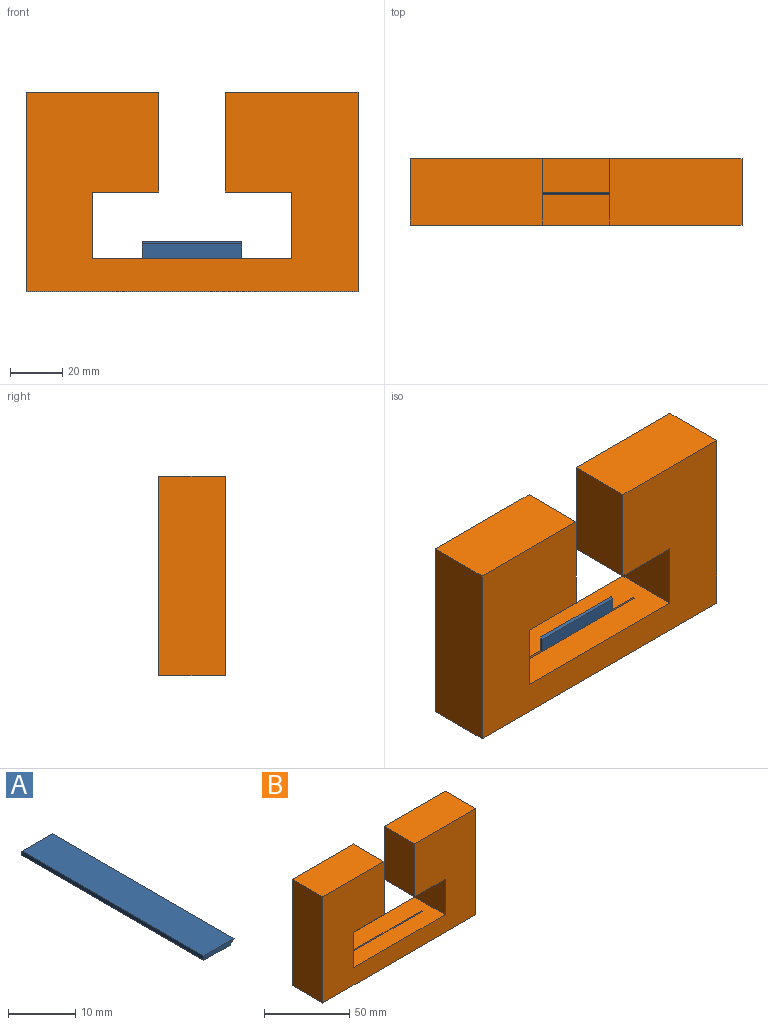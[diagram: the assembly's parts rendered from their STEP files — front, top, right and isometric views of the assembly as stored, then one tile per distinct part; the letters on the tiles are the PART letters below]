
ASSEMBLY  parts=2 mates=1
PART A: 7 faces, bbox 6.4x38.1x0.8 mm
  f0: plane 38.1x0.79mm, normal (-1,0,0), area 30.2mm2, adj f1,f3,f4,f5
  f1: plane 6.35x0.79mm, normal (0,-1,0), area 4.7mm2, adj f0,f2,f4,f5,f6
  f2: plane 38.1x0.01mm, normal (1,0,0), area 0.2mm2, adj f1,f3,f4,f6
  f3: plane 6.35x0.79mm, normal (0,1,0), area 4.7mm2, adj f0,f2,f4,f5,f6
  f4: plane 38.1x6.35mm, normal (0,0,1), area 241.9mm2, adj f0,f1,f2,f3
  f5: plane 38.1x5.56mm, normal (0,0,-1), area 211.9mm2, adj f0,f1,f3,f6
  f6: plane 38.1x0.79mm, normal (0.71,0,-0.71), area 42.4mm2, adj f1,f2,f3,f5
PART B: 18 faces, bbox 127x25.4x76.2 mm
  f0: plane 127x25.4mm, normal (0,0,-1), area 3176.7mm2, adj f2,f3,f12,f13,f14,f15,f16,f17
  f1: plane 76.2x25.4mm, normal (0,0,1), area 1886.4mm2, adj f7,f8,f12,f13,f14,f15,f16,f17
  f2: plane 76.2x25.4mm, normal (-1,0,0), area 1935.5mm2, adj f0,f11,f12,f13
  f3: plane 76.2x25.4mm, normal (1,0,0), area 1935.5mm2, adj f0,f4,f12,f13
  f4: plane 50.8x25.4mm, normal (0,0,1), area 1290.3mm2, adj f3,f5,f12,f13
  f5: plane 38.1x25.4mm, normal (-1,0,0), area 967.7mm2, adj f4,f6,f12,f13
  f6: plane 25.4x25.4mm, normal (0,0,-1), area 645.2mm2, adj f5,f7,f12,f13
  f7: plane 25.4x25.4mm, normal (-1,0,0), area 645.2mm2, adj f1,f6,f12,f13
  f8: plane 25.4x25.4mm, normal (1,0,0), area 645.2mm2, adj f1,f9,f12,f13
  f9: plane 25.4x25.4mm, normal (0,0,-1), area 645.2mm2, adj f8,f10,f12,f13
  f10: plane 38.1x25.4mm, normal (1,0,0), area 967.7mm2, adj f9,f11,f12,f13
  f11: plane 50.8x25.4mm, normal (0,0,1), area 1290.3mm2, adj f2,f10,f12,f13
  f12: plane 127x76.2mm, normal (0,-1,0), area 6774.2mm2, adj f0,f1,f2,f3,f4,f5,f6,f7
  f13: plane 127x76.2mm, normal (0,1,0), area 6774.2mm2, adj f0,f1,f2,f3,f4,f5,f6,f7
  f14: plane 12.7x0.79mm, normal (-1,0,0), area 10.1mm2, adj f0,f1,f15,f17
  f15: plane 61.8x12.7mm, normal (0,1,0), area 784.8mm2, adj f0,f1,f14,f16
  f16: plane 12.7x0.79mm, normal (1,0,0), area 10.1mm2, adj f0,f1,f15,f17
  f17: plane 61.8x12.7mm, normal (0,-1,0), area 784.8mm2, adj f0,f1,f14,f16
PLACE A rot(axis=(-0.58,-0.58,-0.58),120deg) t=(8.9,22.17,-15.16)mm
PLACE B t=(-35.55,35.66,-27.86)mm
MATE fastened A.f4 <-> B.f17  axis (0,1,0) through (8.9,22.96,-11.98)mm
